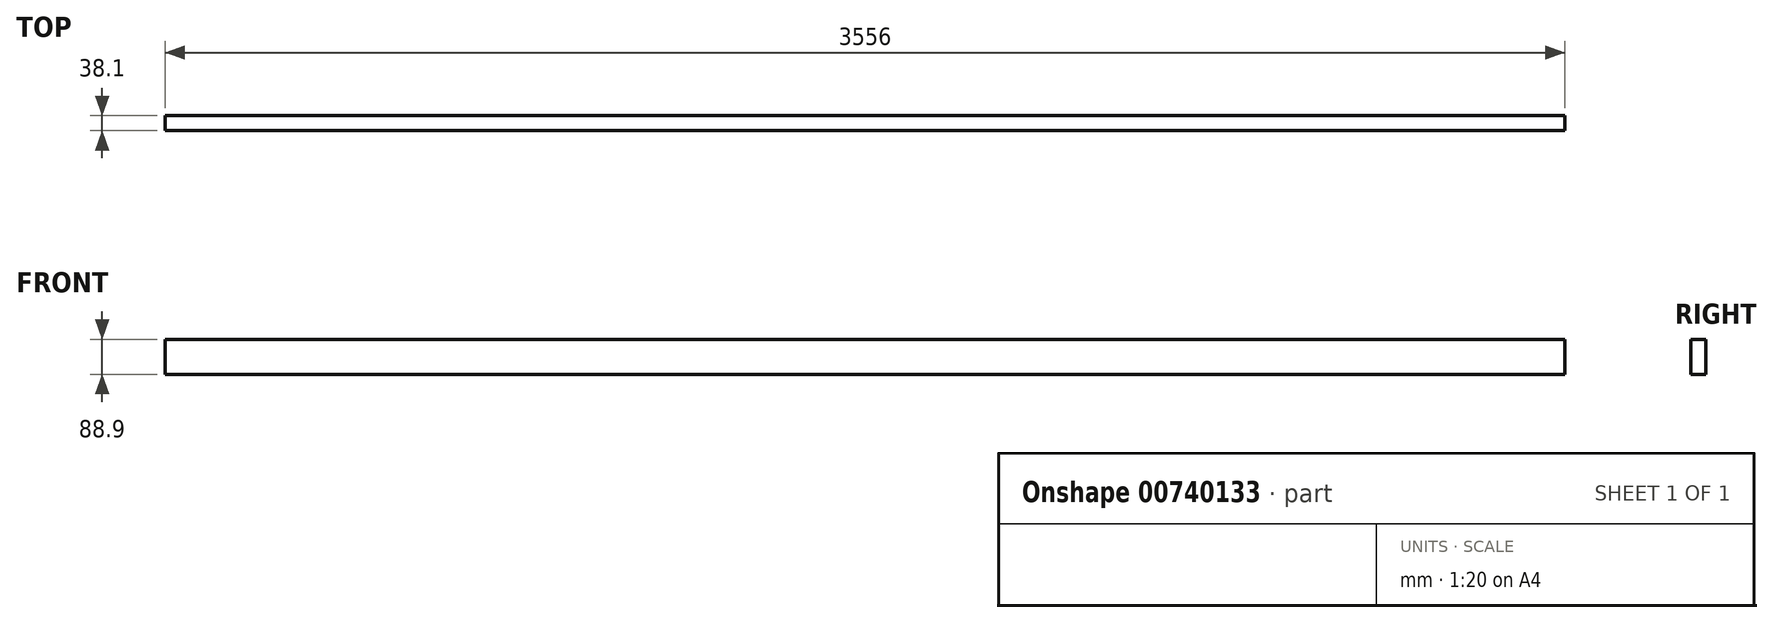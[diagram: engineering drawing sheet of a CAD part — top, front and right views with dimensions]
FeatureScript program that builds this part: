
annotation { "Feature Type Name" : "Feature", "Feature Type Description" : "" }
export const myFeature = defineFeature(function(context is Context, id is Id, definition is map)
    precondition{}
    {
        {
            var Q0;
            Q0=qCreatedBy(makeId("Right.planeOp"),FACE);
            var sketch = newSketch(context, id + "F0", { "sketchPlane" : qUnion([Q0])});
            skLineSegment(sketch, "E0.bottom", {"start": v(-79.68, 85.36) * mm, "end": v(-41.58, 85.36) * mm});
            skLineSegment(sketch, "E0.top", {"start": v(-79.68, -3.54) * mm, "end": v(-41.58, -3.54) * mm});
            skLineSegment(sketch, "E0.left", {"start": v(-79.68, 85.36) * mm, "end": v(-79.68, -3.54) * mm});
            skLineSegment(sketch, "E0.right", {"start": v(-41.58, 85.36) * mm, "end": v(-41.58, -3.54) * mm});
            skSolve(sketch);
        }
        {
            var Q0;
            Q0=makeQuery(id+"F0.imprint","IMPRINT",FACE,{"disambiguationData":[TD([[makeQuery(id+"F0.imprint","IMPRINT",EDGE,{"derivedFrom":sQuery(id+"F0.wireOp",EDGE,"E0.bottom")}),-1.0]])]});
            extrude(context, id + "F1", {"entities" : qUnion([Q0]), "depth" : 3556 * mm, "offsetDistance" : 25.4 * mm});
        }
    });
